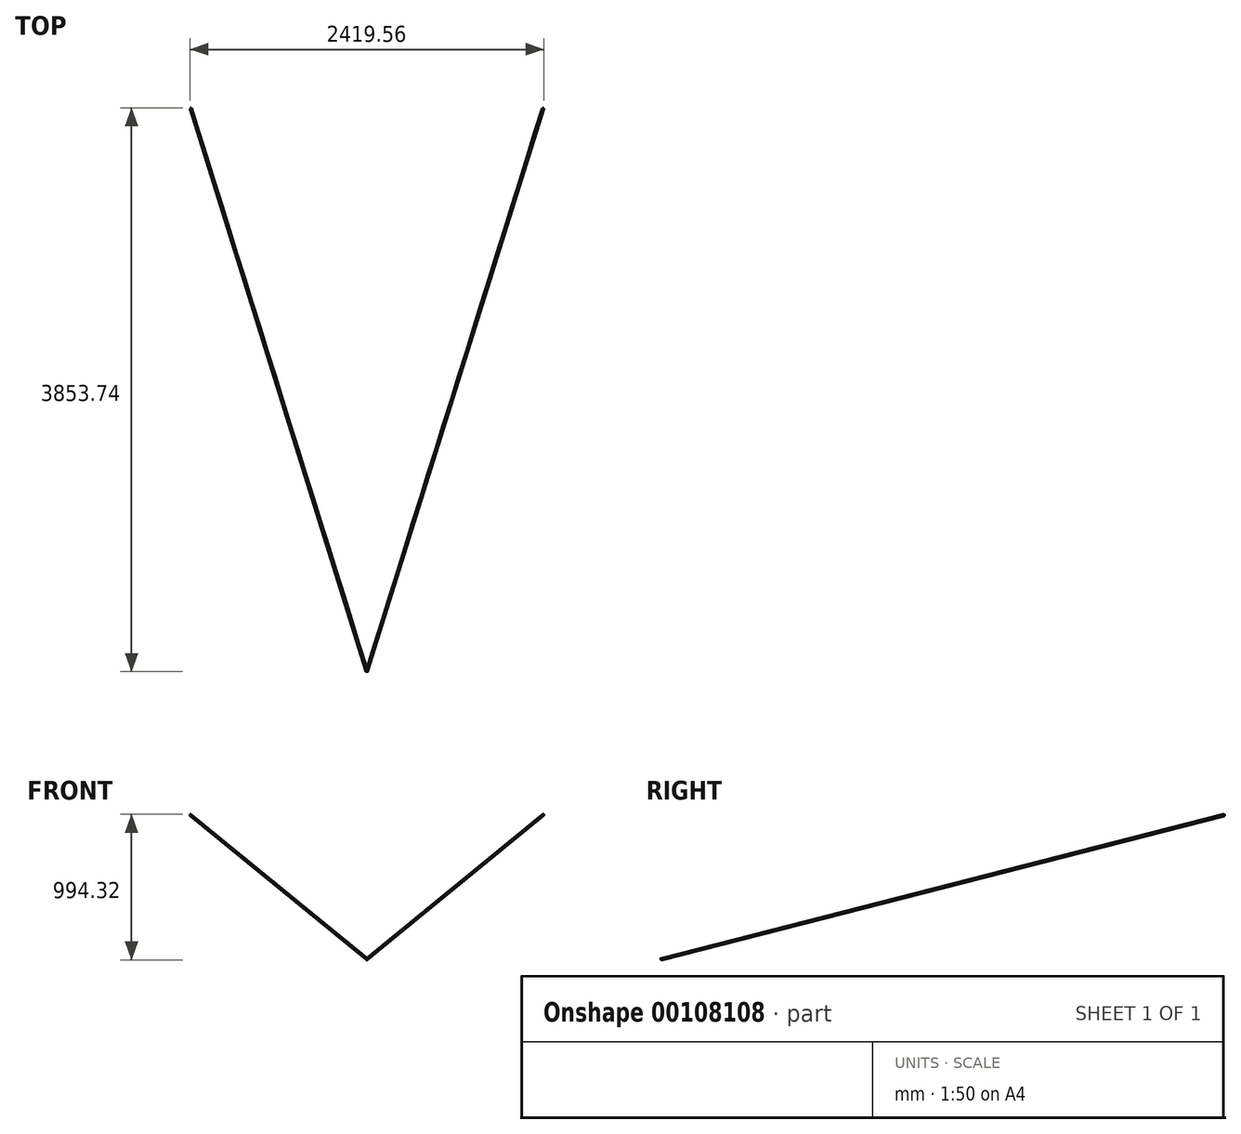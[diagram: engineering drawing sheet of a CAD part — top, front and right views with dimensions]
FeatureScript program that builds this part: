
annotation { "Feature Type Name" : "Feature", "Feature Type Description" : "" }
export const myFeature = defineFeature(function(context is Context, id is Id, definition is map)
    precondition{}
    {
        {
            assignVariable(context, id + "F0", {"name" : "Y1", "anyValue" : 0});
        }
        {
            var Q0;
            Q0=qCreatedBy(makeId("Front.planeOp"),FACE);
            cPlane(context, id + "F1", {"entities" : qUnion([Q0]), "cplaneType" : CPlaneType.OFFSET, "offset" : (getVariable(context, 'Y1')) * mm, "width" : 150 * mm, "height" : 150 * mm});
        }
        {
            var Q0;
            Q0=qCreatedBy(id+"F1.planeOp",FACE);
            var sketch = newSketch(context, id + "F2", { "sketchPlane" : qUnion([Q0])});
            skPoint(sketch, "E0", {"position": v(-1205, 5800) * mm});
            skPoint(sketch, "E1", {"position": v(-1205, 0) * mm});
            skSolve(sketch);
        }
        {
            assignVariable(context, id + "F3", {"name" : "Y2", "anyValue" : 3850});
        }
        {
            var Q0;
            Q0=qCreatedBy(makeId("Front.planeOp"),FACE);
            cPlane(context, id + "F4", {"entities" : qUnion([Q0]), "cplaneType" : CPlaneType.OFFSET, "offset" : (getVariable(context, 'Y2')) * mm, "width" : 150 * mm, "height" : 150 * mm});
        }
        {
            var Q0;
            Q0=qCreatedBy(id+"F4.planeOp",FACE);
            var sketch = newSketch(context, id + "F5", { "sketchPlane" : qUnion([Q0])});
            skPoint(sketch, "E2", {"position": v(0, 4815.4) * mm});
            skSolve(sketch);
        }
        {
            var Q0;
            Q0=sQuery(id+"F2.wireOp",VERTEX,"E0");
            var Q1;
            Q1=sQuery(id+"F2.wireOp",VERTEX,"E1");
            var Q2;
            Q2=sQuery(id+"F5.wireOp",VERTEX,"E2");
            cPlane(context, id + "F6", {"entities" : qUnion([Q0, Q1, Q2]), "cplaneType" : CPlaneType.THREE_POINT, "offset" : 25 * mm, "width" : 150 * mm, "height" : 150 * mm});
        }
        {
            var Q0;
            Q0=qCreatedBy(id+"F6.planeOp",FACE);
            var sketch = newSketch(context, id + "F7", { "sketchPlane" : qUnion([Q0])});
            skPoint(sketch, "E3.0", {"position": v(359.93, 5800) * mm});
            skPoint(sketch, "E4.0", {"position": v(-3674.24, 4815.4) * mm});
            skLineSegment(sketch, "E5", {"start": v(359.93, 5800) * mm, "end": v(-3674.24, 4815.4) * mm});
            skSolve(sketch);
        }
        {
            var Q0;
            Q0=sQuery(id+"F7.wireOp",VERTEX,"E3.0");
            var Q1;
            Q1=sQuery(id+"F7.wireOp",EDGE,"E5");
            cPlane(context, id + "F8", {"entities" : qUnion([Q0, Q1]), "cplaneType" : CPlaneType.LINE_POINT, "offset" : 25 * mm, "width" : 150 * mm, "height" : 150 * mm});
        }
        {
            var Q0;
            Q0=qCreatedBy(id+"F8.planeOp",FACE);
            var sketch = newSketch(context, id + "F9", { "sketchPlane" : qUnion([Q0])});
            skPoint(sketch, "E6.0", {"position": v(-736.15, 5619.16) * mm});
            skCircle(sketch, "E7", {"center": v(-736.15, 5619.16) * mm, "radius": 5 * mm});
            skSolve(sketch);
        }
        {
            var Q0;
            Q0=makeQuery(id+"F9.imprint","IMPRINT",FACE,{"disambiguationData":[TD([[makeQuery(id+"F9.imprint","IMPRINT",EDGE,{"derivedFrom":sQuery(id+"F9.wireOp",EDGE,"E7")}),1.0]])]});
            var Q1;
            Q1=sQuery(id+"F7.wireOp",EDGE,"E5");
            sweep(context, id + "F10", {"profiles" : qUnion([Q0]), "path" : qUnion([Q1])});
        }
        {
            var Q0;
            Q0=makeQuery(id+"F10.opSweep","SWEPT_BODY",BODY,{"disambiguationData":[OSD([sQuery(id+"F7.wireOp",EDGE,"E5"),sQuery(id+"F9.wireOp",EDGE,"E7")])]});
            var Q1;
            Q1=qCreatedBy(makeId("Right.planeOp"),FACE);
            mirror(context, id + "F11", {"operationType" : NewBodyOperationType.ADD, "entities" : qUnion([Q0]), "mirrorPlane" : qUnion([Q1])});
        }
    });
